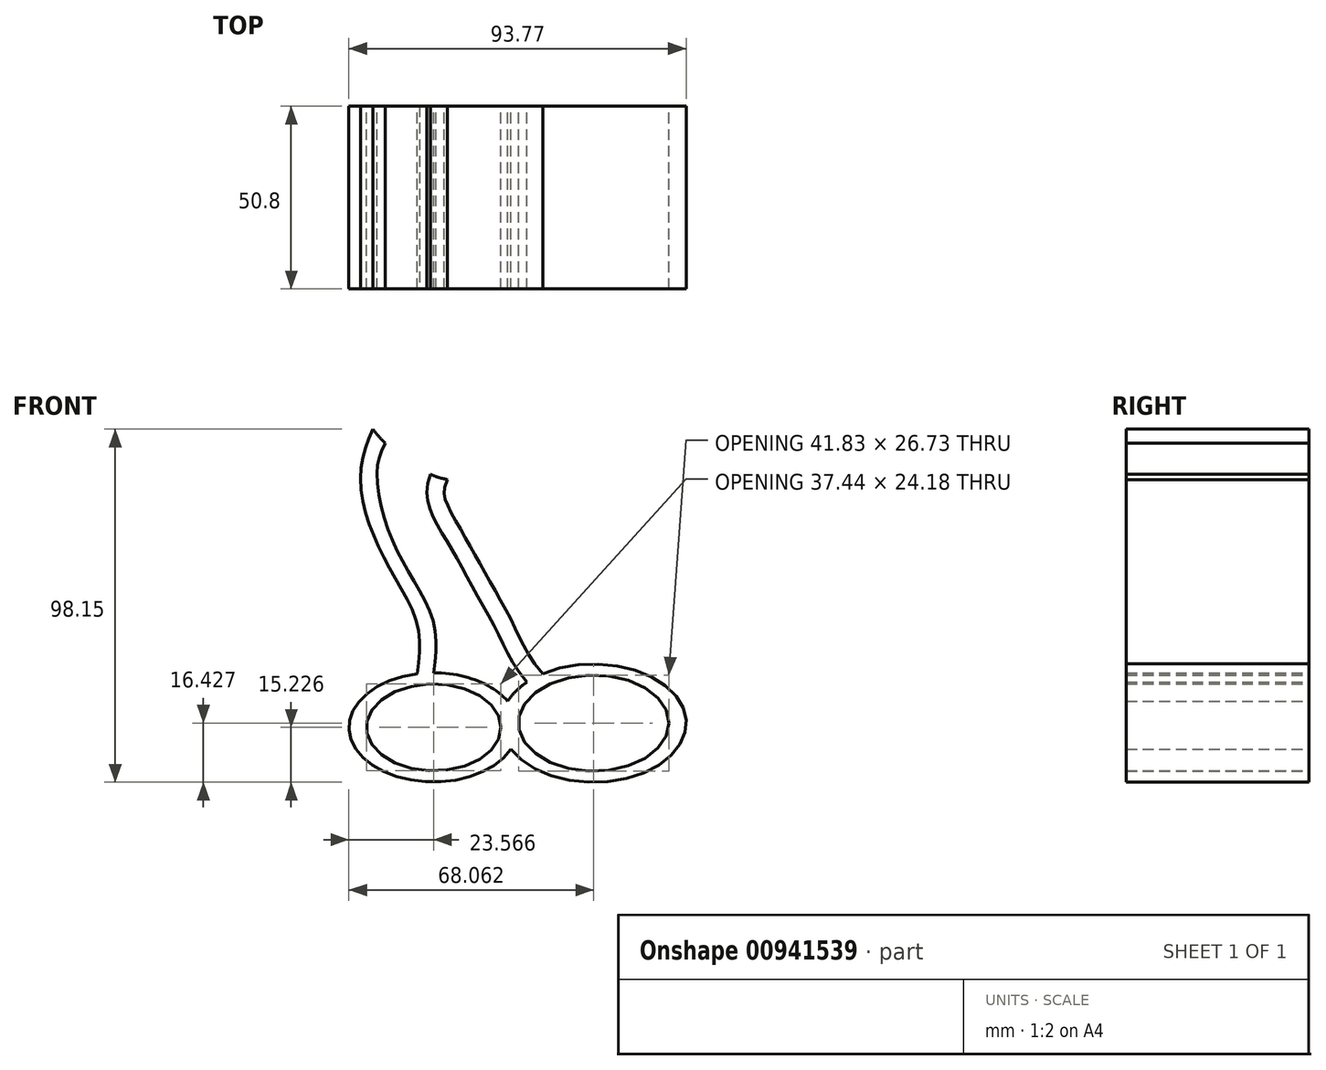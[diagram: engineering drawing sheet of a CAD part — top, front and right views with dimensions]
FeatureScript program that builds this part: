
annotation { "Feature Type Name" : "Feature", "Feature Type Description" : "" }
export const myFeature = defineFeature(function(context is Context, id is Id, definition is map)
    precondition{}
    {
        {
            var Q0;
            Q0=qCreatedBy(makeId("Front.planeOp"),FACE);
            var sketch = newSketch(context, id + "F0", { "sketchPlane" : qUnion([Q0])});
            skEllipse(sketch, "E0", {"center": v(-24.37, 10.92) * mm, "majorRadius": 23.51 * mm, "minorRadius": 15.19 * mm, "majorAxis": v(1, 0)});
            skEllipse(sketch, "E1", {"center": v(20.18, 12.12) * mm, "majorRadius": 20.91 * mm, "minorRadius": 13.36 * mm, "majorAxis": v(1, 0)});
            skEllipse(sketch, "E2", {"center": v(-24.31, 10.92) * mm, "majorRadius": 18.72 * mm, "minorRadius": 12.1 * mm, "majorAxis": v(1, 0)});
            skEllipse(sketch, "E3", {"center": v(20.18, 12.12) * mm, "majorRadius": 25.71 * mm, "minorRadius": 16.43 * mm, "majorAxis": v(1, 0)});
            skFitSpline(sketch, "E4", {"points": [v(-28.9, 25.82) * mm, v(-28.8, 39.18) * mm, v(-35.33, 52.96) * mm, v(-42.4, 68) * mm, v(-44.57, 82.87) * mm, v(-41.13, 94.1) * mm], "startDerivative": vector(8.44, 70.1) * mm, "endDerivative": vector(25.17, 59.33) * mm});
            skFitSpline(sketch, "E5", {"points": [v(6, 25.82) * mm, v(-1.98, 39.18) * mm, v(-9.4, 52.78) * mm, v(-16.11, 64.74) * mm, v(-21, 73.99) * mm, v(-20.47, 79.84) * mm], "startDerivative": vector(-57.3, 66.34) * mm, "endDerivative": vector(25.17, 59.33) * mm});
            skFitSpline(sketch, "E6", {"points": [v(-24.31, 26.1) * mm, v(-24.22, 39.47) * mm, v(-30.75, 53.24) * mm, v(-37.82, 68.29) * mm, v(-40, 83.15) * mm, v(-37.68, 90.31) * mm], "startDerivative": vector(8.44, 70.1) * mm, "endDerivative": vector(25.17, 59.33) * mm});
            skFitSpline(sketch, "E7", {"points": [v(1.63, 23.5) * mm, v(-6.34, 36.86) * mm, v(-13.77, 50.45) * mm, v(-20.48, 62.41) * mm, v(-25.37, 71.66) * mm, v(-25.17, 81.25) * mm], "startDerivative": vector(-57.3, 66.34) * mm, "endDerivative": vector(25.17, 59.33) * mm});
            skFitSpline(sketch, "E8", {"points": [v(-43.52, 104.01) * mm, v(-32.7, 85.66) * mm, v(-13.45, 81.52) * mm, v(-8.54, 105.9) * mm, v(-15.85, 112.52) * mm, v(-43.52, 104.01) * mm]});
            skFitSpline(sketch, "E9.0", {"points": [v(-39.04, 101.62) * mm, v(-39.07, 101.56) * mm, v(-39.09, 101.52) * mm, v(-39.11, 101.47) * mm, v(-39.14, 101.39) * mm, v(-39.17, 101.22) * mm, v(-39.16, 100.82) * mm, v(-39.01, 100.16) * mm, v(-38.67, 99.3) * mm, v(-37.95, 97.92) * mm, v(-36.52, 95.94) * mm, v(-34.16, 93.42) * mm, v(-31.35, 90.97) * mm, v(-28.33, 88.73) * mm, v(-25.33, 86.9) * mm, v(-22.52, 85.57) * mm, v(-20.49, 84.97) * mm, v(-19.18, 84.79) * mm, v(-18.38, 84.77) * mm, v(-17.78, 84.86) * mm, v(-17.34, 85) * mm, v(-17.06, 85.14) * mm, v(-16.83, 85.3) * mm, v(-16.6, 85.5) * mm, v(-16.21, 85.94) * mm, v(-15.68, 86.76) * mm, v(-15.14, 87.85) * mm, v(-14.47, 89.6) * mm, v(-13.77, 92.25) * mm, v(-13.25, 95.8) * mm, v(-13.1, 98.77) * mm, v(-13.12, 101) * mm, v(-13.2, 102.57) * mm, v(-13.36, 103.97) * mm, v(-13.56, 105.16) * mm, v(-13.79, 106.03) * mm, v(-14, 106.58) * mm, v(-14.15, 106.84) * mm, v(-14.21, 106.9) * mm, v(-14.24, 106.93) * mm, v(-14.4, 107.03) * mm, v(-14.8, 107.2) * mm, v(-15.55, 107.37) * mm, v(-16.65, 107.5) * mm, v(-18.05, 107.58) * mm, v(-19.68, 107.57) * mm, v(-22.08, 107.44) * mm, v(-25.37, 107.05) * mm, v(-29.4, 106.24) * mm, v(-32.57, 105.3) * mm, v(-34.79, 104.44) * mm, v(-36.25, 103.75) * mm, v(-37.45, 103.06) * mm, v(-38.2, 102.5) * mm, v(-38.62, 102.12) * mm, v(-38.85, 101.87) * mm, v(-38.97, 101.71) * mm, v(-39.04, 101.62) * mm, v(-39.07, 101.56) * mm, v(-39.09, 101.52) * mm, v(-39.04, 101.62) * mm]});
            skSolve(sketch);
        }
        {
            var Q0;
            Q0=makeQuery(id+"F0.imprint","IMPRINT",FACE,{"disambiguationData":[TD([[makeQuery(id+"F0.imprint","IMPRINT",EDGE,{"derivedFrom":sQuery(id+"F0.wireOp",EDGE,"E1")}),-1.0]])]});
            var Q1;
            {var subQ0=sQuery(id+"F0.wireOp",EDGE,"E5");Q1=makeQuery(id+"F0.imprint","IMPRINT",FACE,{"disambiguationData":[TD([[makeQuery(id+"F0.imprint","IMPRINT",EDGE,{"derivedFrom":subQ0}),1.0]])]});}
            var Q2;
            Q2=makeQuery(id+"F0.imprint","IMPRINT",FACE,{"disambiguationData":[TD([[makeQuery(id+"F0.imprint","IMPRINT",EDGE,{"derivedFrom":sQuery(id+"F0.wireOp",EDGE,"E9.0")}),-1.0]])]});
            var Q3;
            {var subQ0=sQuery(id+"F0.wireOp",EDGE,"E4");var subQ1=sQuery(id+"F0.wireOp",EDGE,"E0");var subQ2=makeQuery(id+"F0.imprint","INTERSECT",VERTEX,{"derivedFrom":[subQ1,subQ0]});Q3=makeQuery(id+"F0.imprint","IMPRINT",FACE,{"disambiguationData":[TD([[makeQuery(id+"F0.imprint","IMPRINT",EDGE,{"disambiguationData":[TD([[subQ2,1.0]])],"derivedFrom":subQ1}),-1.0]])]});}
            var Q4;
            {var subQ0=sQuery(id+"F0.wireOp",EDGE,"E3");var subQ1=sQuery(id+"F0.wireOp",EDGE,"E0");var subQ2=makeQuery(id+"F0.imprint","INTERSECT",VERTEX,{"disambiguationData":[OD(0.0)],"derivedFrom":[subQ1,subQ0]});Q4=makeQuery(id+"F0.imprint","IMPRINT",FACE,{"disambiguationData":[TD([[makeQuery(id+"F0.imprint","IMPRINT",EDGE,{"disambiguationData":[TD([[subQ2,-1.0]])],"derivedFrom":subQ1}),1.0]])]});}
            var Q5;
            Q5=makeQuery(id+"F0.imprint","IMPRINT",FACE,{"disambiguationData":[TD([[makeQuery(id+"F0.imprint","IMPRINT",EDGE,{"derivedFrom":sQuery(id+"F0.wireOp",EDGE,"E2")}),-1.0]])]});
            extrude(context, id + "F1", {"entities" : qUnion([Q0, Q1, Q2, Q3, Q4, Q5]), "depth" : 50.8 * mm, "offsetDistance" : 25.4 * mm});
        }
    });
